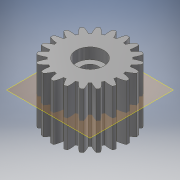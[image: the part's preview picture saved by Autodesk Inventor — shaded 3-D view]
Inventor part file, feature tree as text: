
AUTODESK INVENTOR PART (.ipt)
format: ipt  version: 2017 (Build 210142000, 142)  size: 239,104 bytes
history: native  units: mm (DEFAULTED — no unit token found)
features: plane x4, sketch x4, extrude x3, other x3, mirror x1
ambient origin geometry x8: Origin, YZ Plane, XZ Plane, XY Plane, X Axis, Y Axis, Z Axis, Center Point
bodies: Solid1 (feature_tree)
feature tree (15):
  extrude  "Extrusion1"  Depth=20.0mm TaperAngle=0.0deg
  plane  "Work Plane2"
  plane  "Work Plane8"
  plane  "Work Plane9"
  other  "Spur Gear"
  extrude  "Extrusion2"  Depth=10.0mm TaperAngle=0.0deg
  extrude  "Extrusion3"  Depth=1.570796mm TaperAngle=0.0deg
  plane  "Work Plane11"
  mirror  "Mirror1"
  sketch  "Sketch1"  dims[d0=27.498118mm d1=20.0mm d2=0.0mm]
  sketch  "Sketch2"  dims[d3=24.950495mm d4=10.0mm d5=0.0mm]
  other  "Srf1"
  sketch  "Sketch3"  dims[d16=63.0mm d17=0.0mm d34=1.570796mm]
  sketch  "Sketch4"  dims[d39=0.0mm d41=0.0mm d43=63.0mm d46=63.0mm d47=0.0mm d48=0.0mm d49=10.0mm d50=4.0mm d51=0.0mm d52=6.0mm d53=4.0mm d54=0.0mm]
  other  "Pitch Diameter"
